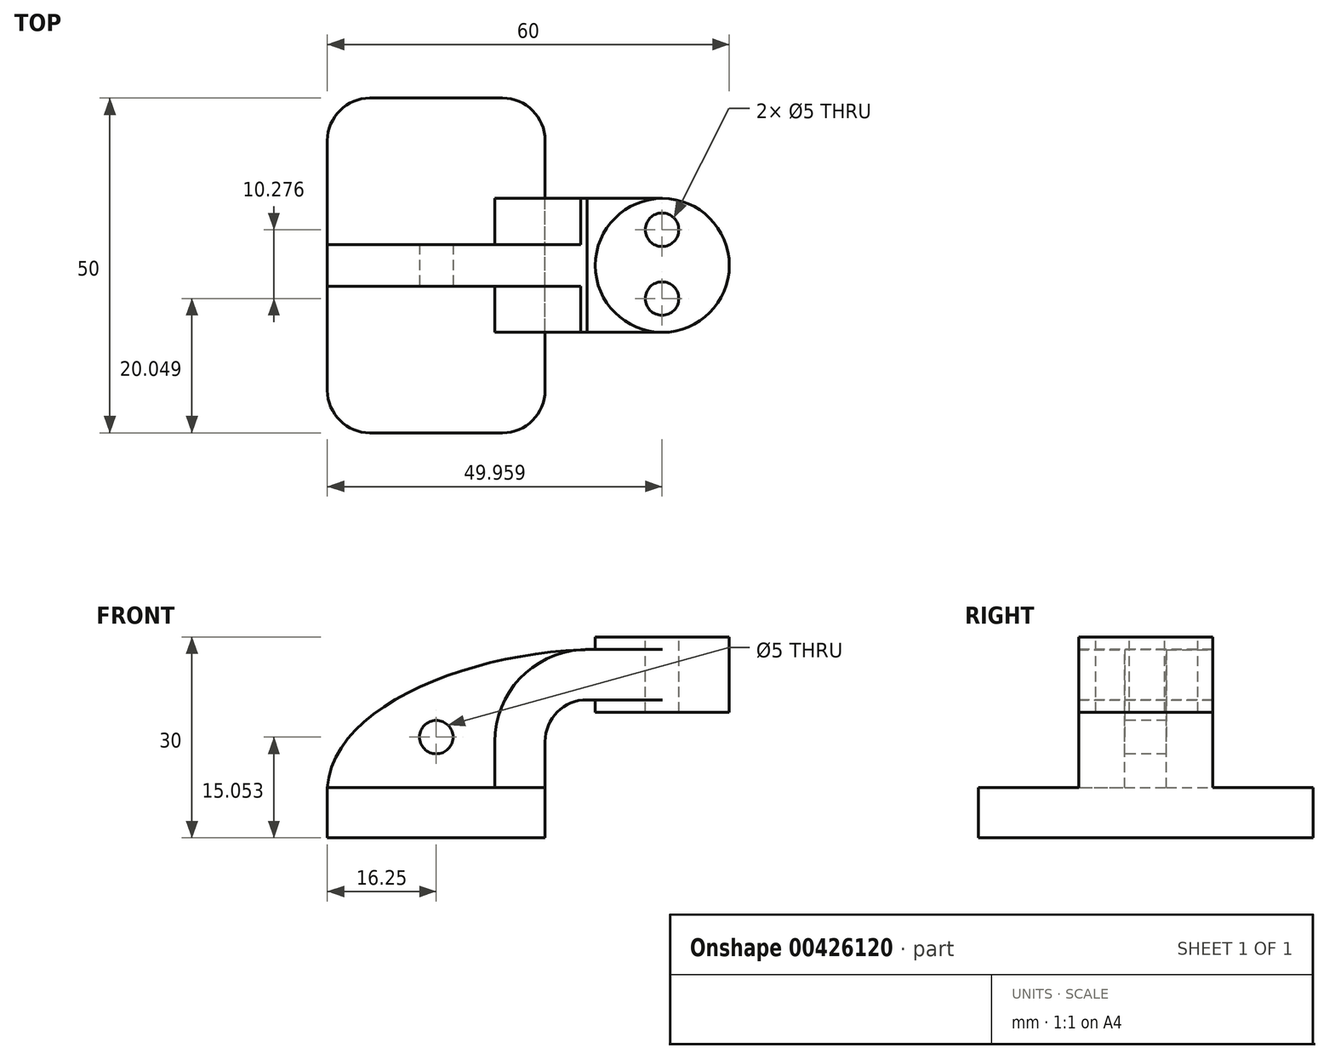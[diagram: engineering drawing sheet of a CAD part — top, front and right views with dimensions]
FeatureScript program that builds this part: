
annotation { "Feature Type Name" : "Feature", "Feature Type Description" : "" }
export const myFeature = defineFeature(function(context is Context, id is Id, definition is map)
    precondition{}
    {
        {
            var Q0;
            Q0=qCreatedBy(makeId("Front.planeOp"),FACE);
            var sketch = newSketch(context, id + "F0", { "sketchPlane" : qUnion([Q0])});
            skLineSegment(sketch, "E0.bottom", {"start": v(-16.25, 3.75) * mm, "end": v(16.25, 3.75) * mm});
            skLineSegment(sketch, "E0.top", {"start": v(-16.25, -3.75) * mm, "end": v(16.25, -3.75) * mm});
            skLineSegment(sketch, "E0.left", {"start": v(-16.25, 3.75) * mm, "end": v(-16.25, -3.75) * mm});
            skLineSegment(sketch, "E0.right", {"start": v(16.25, 3.75) * mm, "end": v(16.25, -3.75) * mm});
            skPoint(sketch, "E0.middle", {"position": v(0, 0) * mm});
            skLineSegment(sketch, "E1.bottom", {"start": v(23.75, 26.25) * mm, "end": v(43.75, 26.25) * mm});
            skLineSegment(sketch, "E1.top", {"start": v(23.75, 15) * mm, "end": v(43.75, 15) * mm});
            skLineSegment(sketch, "E1.left", {"start": v(23.75, 26.25) * mm, "end": v(23.75, 15) * mm});
            skLineSegment(sketch, "E1.right", {"start": v(43.75, 26.25) * mm, "end": v(43.75, 15) * mm});
            skPoint(sketch, "E1.middle", {"position": v(33.75, 20.63) * mm});
            skLineSegment(sketch, "E2", {"start": v(16.25, 3.75) * mm, "end": v(16.25, 10.63) * mm});
            skArc(sketch, "E3", {"start": v(16.25, 10.63) * mm, "mid": v(18.08, 15.05) * mm, "end": v(22.5, 16.88) * mm});
            skLineSegment(sketch, "E4", {"start": v(22.5, 16.88) * mm, "end": v(33.75, 16.88) * mm});
            skLineSegment(sketch, "E5.0", {"start": v(22.5, 24.38) * mm, "end": v(33.75, 24.38) * mm});
            skArc(sketch, "E5.1", {"start": v(8.75, 10.63) * mm, "mid": v(12.78, 20.35) * mm, "end": v(22.5, 24.38) * mm});
            skLineSegment(sketch, "E5.2", {"start": v(8.75, 3.75) * mm, "end": v(8.75, 10.63) * mm});
            skLineSegment(sketch, "E6", {"start": v(33.75, 26.25) * mm, "end": v(33.75, 15) * mm});
            skFitSpline(sketch, "E7", {"points": [v(-16.25, 3.75) * mm, v(22.5, 24.38) * mm], "startDerivative": vector(2.41, 37.3) * mm, "endDerivative": vector(51.22, 1.38) * mm});
            skSolve(sketch);
        }
        {
            var Q0;
            Q0=makeQuery(id+"F0.imprint","IMPRINT",FACE,{"disambiguationData":[TD([[makeQuery(id+"F0.imprint","IMPRINT",EDGE,{"derivedFrom":sQuery(id+"F0.wireOp",EDGE,"E0.top")}),1.0]])]});
            extrude(context, id + "F1", {"entities" : qUnion([Q0]), "endBound" : BoundingType.SYMMETRIC, "depth" : 50 * mm});
        }
        {
            var Q0;
            {var subQ1=sQuery(id+"F0.wireOp",EDGE,"E2");Q0=makeQuery(id+"F0.imprint","IMPRINT",FACE,{"disambiguationData":[TD([[makeQuery(id+"F0.imprint","IMPRINT",EDGE,{"derivedFrom":subQ1}),1.0]])]});}
            var Q1;
            {var subQ0=sQuery(id+"F0.wireOp",EDGE,"E5.0");var subQ1=sQuery(id+"F0.wireOp",EDGE,"E1.left");var subQ2=makeQuery(id+"F0.imprint","INTERSECT",VERTEX,{"derivedFrom":[subQ1,subQ0]});Q1=makeQuery(id+"F0.imprint","IMPRINT",FACE,{"disambiguationData":[TD([[makeQuery(id+"F0.imprint","IMPRINT",EDGE,{"disambiguationData":[TD([[subQ2,-1.0]])],"derivedFrom":subQ1}),1.0]])]});}
            extrude(context, id + "F2", {"entities" : qUnion([Q0, Q1]), "operationType" : NewBodyOperationType.ADD, "endBound" : BoundingType.SYMMETRIC, "depth" : 20 * mm});
        }
        {
            var Q0;
            {var subQ3=sQuery(id+"F0.wireOp",EDGE,"E5.2");Q0=makeQuery(id+"F0.imprint","IMPRINT",FACE,{"disambiguationData":[TD([[makeQuery(id+"F0.imprint","IMPRINT",EDGE,{"derivedFrom":subQ3}),1.0]])]});}
            extrude(context, id + "F3", {"entities" : qUnion([Q0]), "operationType" : NewBodyOperationType.ADD, "endBound" : BoundingType.SYMMETRIC, "depth" : 6.25 * mm});
        }
        {
            var Q0;
            {var subQ4=sQuery(id+"F0.wireOp",EDGE,"E1.right");Q0=makeQuery(id+"F0.imprint","IMPRINT",FACE,{"disambiguationData":[TD([[makeQuery(id+"F0.imprint","IMPRINT",EDGE,{"derivedFrom":subQ4}),-1.0]])]});}
            var Q1;
            Q1=sQuery(id+"F0.wireOp",EDGE,"E6");
            revolve(context, id + "F4", {"operationType" : NewBodyOperationType.ADD, "entities" : qUnion([Q0]), "axis" : qUnion([Q1]), "revolveType" : RevolveType.FULL});
        }
        {
            var Q0;
            Q0=makeQuery(id+"F1.opExtrude","CAP_EDGE",EDGE,{"disambiguationData":[OSD([sQuery(id+"F0.wireOp",EDGE,"E0.left")])],"isStart":false});
            var Q1;
            Q1=makeQuery(id+"F1.opExtrude","CAP_EDGE",EDGE,{"disambiguationData":[OSD([sQuery(id+"F0.wireOp",EDGE,"E0.right")])],"isStart":false});
            var Q2;
            Q2=makeQuery(id+"F1.opExtrude","CAP_EDGE",EDGE,{"disambiguationData":[OSD([sQuery(id+"F0.wireOp",EDGE,"E0.right")])],"isStart":true});
            var Q3;
            Q3=makeQuery(id+"F1.opExtrude","CAP_EDGE",EDGE,{"disambiguationData":[OSD([sQuery(id+"F0.wireOp",EDGE,"E0.left")])],"isStart":true});
            fillet(context, id + "F5", {"entities" : qUnion([Q0, Q1, Q2, Q3]), "radius" : 6.35 * mm, "tangentPropagation" : true, "allowEdgeOverflow" : false});
        }
        {
            var Q0;
            Q0=makeQuery(id+"F4.opRevolve","SWEPT_FACE",FACE,{"disambiguationData":[OSD([sQuery(id+"F0.wireOp",EDGE,"E1.bottom")])]});
            var sketch = newSketch(context, id + "F6", { "sketchPlane" : qUnion([Q0])});
            skPoint(sketch, "E8", {"position": v(33.7, 5.32) * mm});
            skPoint(sketch, "E9", {"position": v(33.7, -4.95) * mm});
            skSolve(sketch);
        }
        {
            var Q0;
            Q0=sQuery(id+"F6.wireOp",VERTEX,"E8");
            var Q1;
            Q1=sQuery(id+"F6.wireOp",VERTEX,"E9");
            var Q2;
            Q2=makeQuery(id+"F1.opExtrude","SWEPT_BODY",BODY,{"disambiguationData":[OSD([sQuery(id+"F0.wireOp",EDGE,"E0.bottom"),sQuery(id+"F0.wireOp",EDGE,"E0.top"),sQuery(id+"F0.wireOp",EDGE,"E0.left"),sQuery(id+"F0.wireOp",EDGE,"E0.right")])]});
            hole(context, id + "F7", {"style" : HoleStyle.SIMPLE, "endStyle" : HoleEndStyle.THROUGH, "holeDiameter" : 5 * mm, "isTappedThrough" : true, "tappedDepth" : 12.7 * mm, "tapClearance" : 3, "locations" : qUnion([Q0, Q1]), "scope" : qUnion([Q2])});
        }
        {
            var Q0;
            Q0=makeQuery(id+"F3.opExtrude","CAP_FACE",FACE,{"disambiguationData":[OSD([sQuery(id+"F0.wireOp",EDGE,"E0.bottom"),sQuery(id+"F0.wireOp",EDGE,"E5.1"),sQuery(id+"F0.wireOp",EDGE,"E5.2"),sQuery(id+"F0.wireOp",EDGE,"E7")])],"isStart":false});
            var sketch = newSketch(context, id + "F8", { "sketchPlane" : qUnion([Q0])});
            skPoint(sketch, "E10", {"position": v(0, 11.3) * mm});
            skSolve(sketch);
        }
        {
            var Q0;
            Q0=sQuery(id+"F8.wireOp",VERTEX,"E10");
            var Q1;
            Q1=makeQuery(id+"F1.opExtrude","SWEPT_BODY",BODY,{"disambiguationData":[OSD([sQuery(id+"F0.wireOp",EDGE,"E0.bottom"),sQuery(id+"F0.wireOp",EDGE,"E0.top"),sQuery(id+"F0.wireOp",EDGE,"E0.left"),sQuery(id+"F0.wireOp",EDGE,"E0.right")])]});
            hole(context, id + "F9", {"style" : HoleStyle.SIMPLE, "endStyle" : HoleEndStyle.THROUGH, "holeDiameter" : 5 * mm, "isTappedThrough" : true, "tappedDepth" : 12.7 * mm, "tapClearance" : 3, "locations" : qUnion([Q0]), "scope" : qUnion([Q1])});
        }
    });
